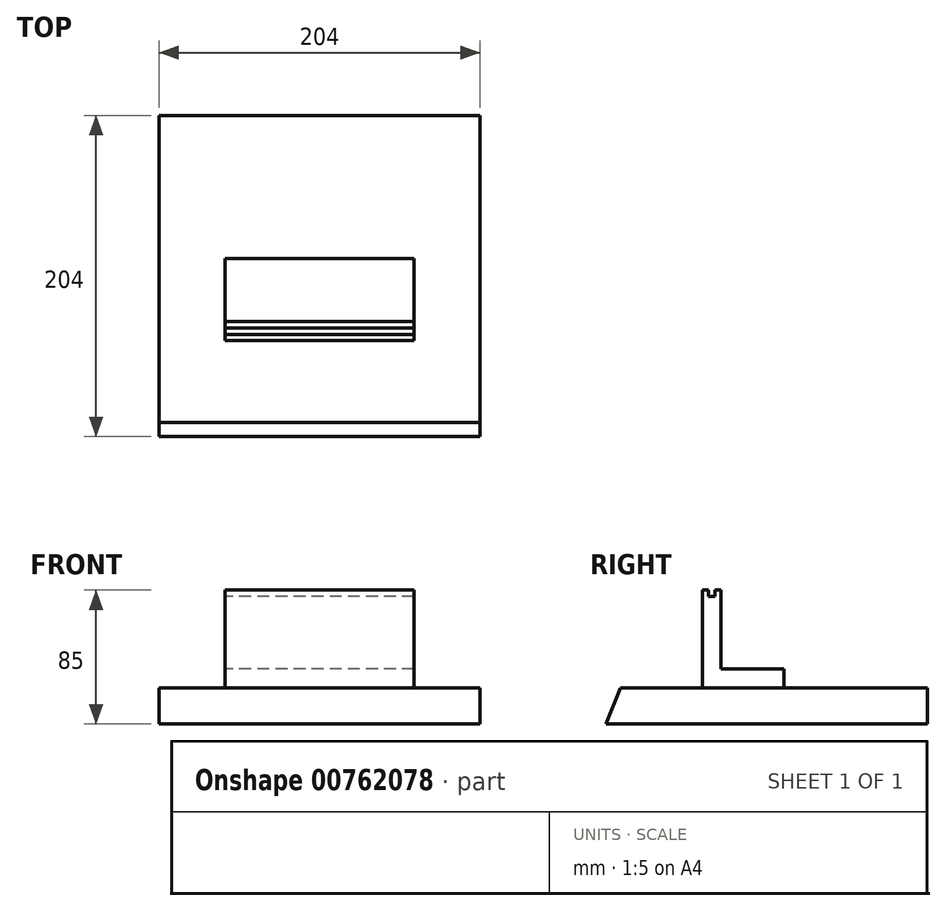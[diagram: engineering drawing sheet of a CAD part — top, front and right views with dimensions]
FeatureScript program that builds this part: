
annotation { "Feature Type Name" : "Feature", "Feature Type Description" : "" }
export const myFeature = defineFeature(function(context is Context, id is Id, definition is map)
    precondition{}
    {
        {
            var Q0;
            Q0=qCreatedBy(makeId("Right.planeOp"),FACE);
            var sketch = newSketch(context, id + "F0", { "sketchPlane" : qUnion([Q0])});
            skLineSegment(sketch, "E0", {"start": v(0, 0) * mm, "end": v(204, 0) * mm});
            skLineSegment(sketch, "E1", {"start": v(204, 0) * mm, "end": v(204, 23) * mm});
            skLineSegment(sketch, "E2", {"start": v(204, 23) * mm, "end": v(9, 23) * mm});
            skLineSegment(sketch, "E3", {"start": v(9, 23) * mm, "end": v(0, 0) * mm});
            skLineSegment(sketch, "E4", {"start": v(61, 23) * mm, "end": v(61, 85) * mm});
            skLineSegment(sketch, "E5", {"start": v(61, 85) * mm, "end": v(65, 85) * mm});
            skLineSegment(sketch, "E6", {"start": v(73, 85) * mm, "end": v(73, 35) * mm});
            skLineSegment(sketch, "E7", {"start": v(73, 35) * mm, "end": v(113, 35) * mm});
            skLineSegment(sketch, "E8", {"start": v(113, 35) * mm, "end": v(113, 23) * mm});
            skLineSegment(sketch, "E9.bottom", {"start": v(69, 81) * mm, "end": v(65, 81) * mm});
            skLineSegment(sketch, "E9.left", {"start": v(69, 81) * mm, "end": v(69, 85) * mm});
            skLineSegment(sketch, "E9.right", {"start": v(65, 81) * mm, "end": v(65, 85) * mm});
            skPoint(sketch, "E9.middle", {"position": v(67, 85) * mm});
            skLineSegment(sketch, "E10.trimOffspring", {"start": v(69, 85) * mm, "end": v(73, 85) * mm});
            skPoint(sketch, "E9.top.end.orphan", {"position": v(65, 89) * mm});
            skPoint(sketch, "E9.top.start.orphan", {"position": v(69, 89) * mm});
            skPoint(sketch, "E11.startSnap0", {"position": v(102, 0) * mm});
            skSolve(sketch);
        }
        {
            var Q0;
            Q0=makeQuery(id+"F0.imprint","IMPRINT",FACE,{"disambiguationData":[TD([[makeQuery(id+"F0.imprint","IMPRINT",EDGE,{"derivedFrom":sQuery(id+"F0.wireOp",EDGE,"E0")}),1.0]])]});
            extrude(context, id + "F1", {"entities" : qUnion([Q0]), "endBound" : BoundingType.SYMMETRIC, "depth" : 204 * mm, "offsetDistance" : 25 * mm});
        }
        {
            var Q0;
            {var subQ0=sQuery(id+"F0.wireOp",EDGE,"E4");Q0=makeQuery(id+"F0.imprint","IMPRINT",FACE,{"disambiguationData":[TD([[makeQuery(id+"F0.imprint","IMPRINT",EDGE,{"derivedFrom":subQ0}),-1.0]])]});}
            extrude(context, id + "F2", {"entities" : qUnion([Q0]), "operationType" : NewBodyOperationType.ADD, "endBound" : BoundingType.SYMMETRIC, "depth" : 120 * mm, "offsetDistance" : 25 * mm});
        }
    });
